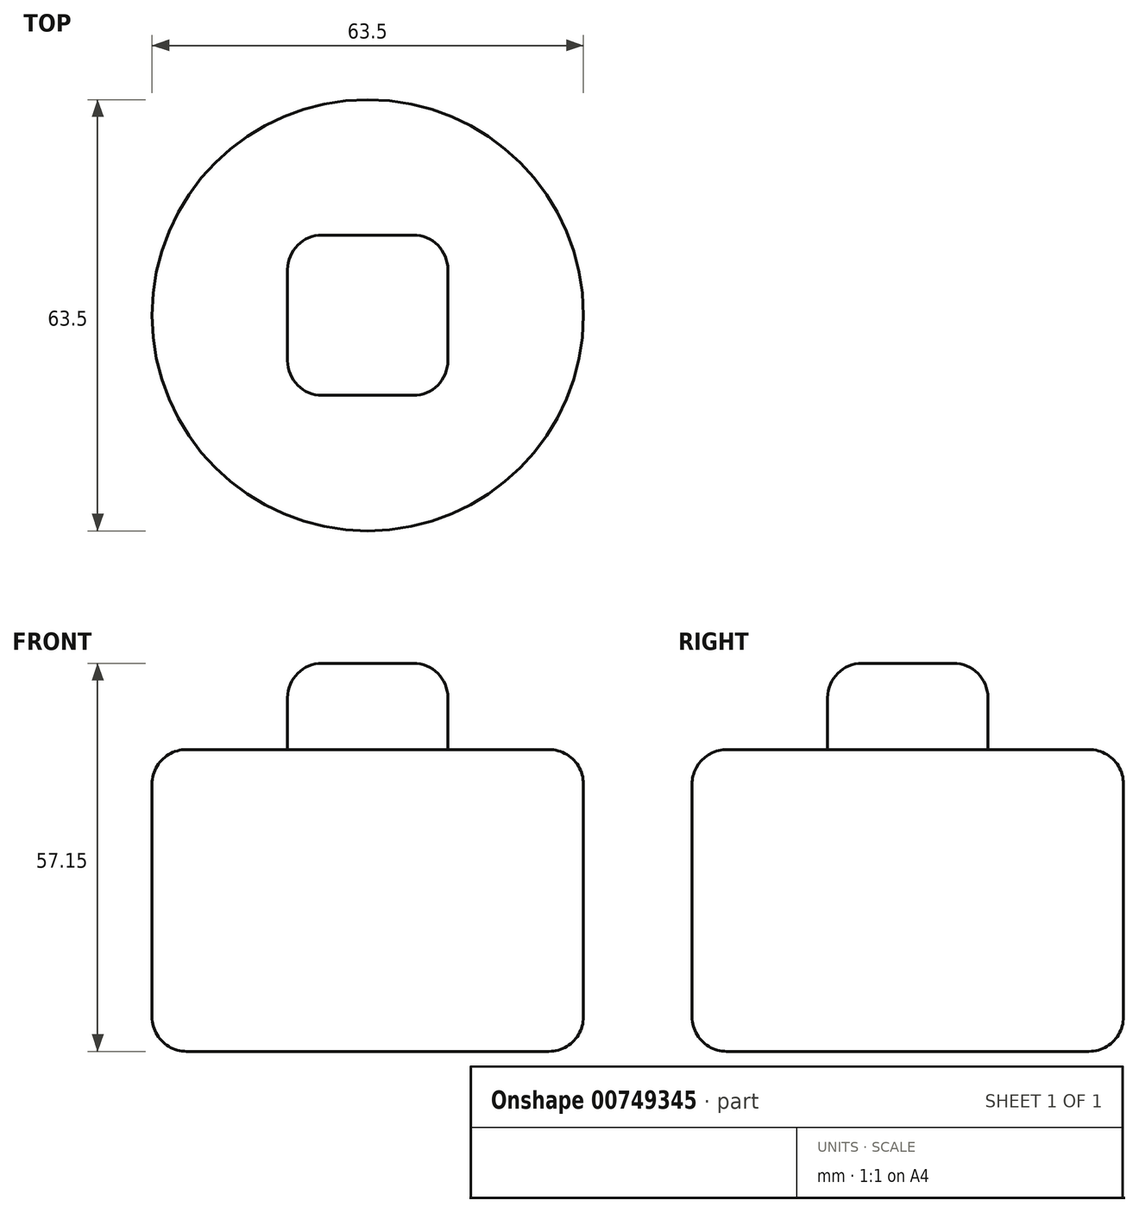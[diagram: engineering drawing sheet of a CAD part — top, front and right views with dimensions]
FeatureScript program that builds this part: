
annotation { "Feature Type Name" : "Feature", "Feature Type Description" : "" }
export const myFeature = defineFeature(function(context is Context, id is Id, definition is map)
    precondition{}
    {
        {
            var Q0;
            Q0=qCreatedBy(makeId("Top.planeOp"),FACE);
            var sketch = newSketch(context, id + "F0", { "sketchPlane" : qUnion([Q0])});
            skCircle(sketch, "E0", {"center": v(-28.48, 7.65) * mm, "radius": 31.75 * mm});
            skSolve(sketch);
        }
        {
            var Q0;
            Q0=makeQuery(id+"F0.imprint","IMPRINT",FACE,{"disambiguationData":[TD([[makeQuery(id+"F0.imprint","IMPRINT",EDGE,{"derivedFrom":sQuery(id+"F0.wireOp",EDGE,"E0")}),1.0]])]});
            extrude(context, id + "F1", {"entities" : qUnion([Q0]), "depth" : 44.45 * mm, "offsetDistance" : 25.4 * mm});
        }
        {
            var Q0;
            Q0=makeQuery(id+"F1.opExtrude","CAP_FACE",FACE,{"disambiguationData":[OSD([sQuery(id+"F0.wireOp",EDGE,"E0")])],"isStart":false});
            var sketch = newSketch(context, id + "F2", { "sketchPlane" : qUnion([Q0])});
            skCircle(sketch, "E1.cCircle", {"center": v(-28.48, 7.65) * mm, "radius": 11.8 * mm, "construction": true});
            skLineSegment(sketch, "E1.0", {"start": v(-16.68, -4.15) * mm, "end": v(-40.28, -4.15) * mm});
            skLineSegment(sketch, "E1.1", {"start": v(-40.28, -4.15) * mm, "end": v(-40.28, 19.45) * mm});
            skLineSegment(sketch, "E1.2", {"start": v(-40.28, 19.45) * mm, "end": v(-16.68, 19.45) * mm});
            skLineSegment(sketch, "E1.3", {"start": v(-16.68, 19.45) * mm, "end": v(-16.68, -4.15) * mm});
            skPoint(sketch, "E1.0.midPoint", {"position": v(-28.48, -4.15) * mm});
            skSolve(sketch);
        }
        {
            var Q0;
            Q0=makeQuery(id+"F2.imprint","IMPRINT",FACE,{"disambiguationData":[TD([[makeQuery(id+"F2.imprint","IMPRINT",EDGE,{"derivedFrom":sQuery(id+"F2.wireOp",EDGE,"E1.0")}),-1.0]])]});
            extrude(context, id + "F3", {"entities" : qUnion([Q0]), "operationType" : NewBodyOperationType.ADD, "depth" : 12.7 * mm, "offsetDistance" : 25.4 * mm});
        }
        {
            var Q0;
            Q0=makeQuery(id+"F1.opExtrude","CAP_EDGE",EDGE,{"disambiguationData":[OSD([sQuery(id+"F0.wireOp",EDGE,"E0")])],"isStart":false});
            var Q1;
            Q1=makeQuery(id+"F1.opExtrude","CAP_EDGE",EDGE,{"disambiguationData":[OSD([sQuery(id+"F0.wireOp",EDGE,"E0")])],"isStart":true});
            var Q2;
            Q2=makeQuery(id+"F3.opExtrude","CAP_EDGE",EDGE,{"disambiguationData":[OSD([sQuery(id+"F2.wireOp",EDGE,"E1.3")])],"isStart":false});
            var Q3;
            Q3=makeQuery(id+"F3.opExtrude","CAP_EDGE",EDGE,{"disambiguationData":[OSD([sQuery(id+"F2.wireOp",EDGE,"E1.0")])],"isStart":false});
            var Q4;
            Q4=makeQuery(id+"F3.opExtrude","CAP_EDGE",EDGE,{"disambiguationData":[OSD([sQuery(id+"F2.wireOp",EDGE,"E1.1")])],"isStart":false});
            var Q5;
            Q5=makeQuery(id+"F3.opExtrude","CAP_EDGE",EDGE,{"disambiguationData":[OSD([sQuery(id+"F2.wireOp",EDGE,"E1.2")])],"isStart":false});
            var Q6;
            Q6=makeQuery(id+"F3.opExtrude","SWEPT_EDGE",EDGE,{"disambiguationData":[OSD([sQuery(id+"F2.wireOp",EDGE,"E1.0"),sQuery(id+"F2.wireOp",EDGE,"E1.3")])]});
            var Q7;
            Q7=makeQuery(id+"F3.opExtrude","SWEPT_EDGE",EDGE,{"disambiguationData":[OSD([sQuery(id+"F2.wireOp",EDGE,"E1.0"),sQuery(id+"F2.wireOp",EDGE,"E1.1")])]});
            var Q8;
            Q8=makeQuery(id+"F3.opExtrude","SWEPT_EDGE",EDGE,{"disambiguationData":[OSD([sQuery(id+"F2.wireOp",EDGE,"E1.2"),sQuery(id+"F2.wireOp",EDGE,"E1.3")])]});
            var Q9;
            Q9=makeQuery(id+"F3.opExtrude","SWEPT_EDGE",EDGE,{"disambiguationData":[OSD([sQuery(id+"F2.wireOp",EDGE,"E1.1"),sQuery(id+"F2.wireOp",EDGE,"E1.2")])]});
            fillet(context, id + "F4", {"entities" : qUnion([Q0, Q1, Q2, Q3, Q4, Q5, Q6, Q7, Q8, Q9]), "radius" : 5.08 * mm, "tangentPropagation" : true, "allowEdgeOverflow" : false});
        }
    });
